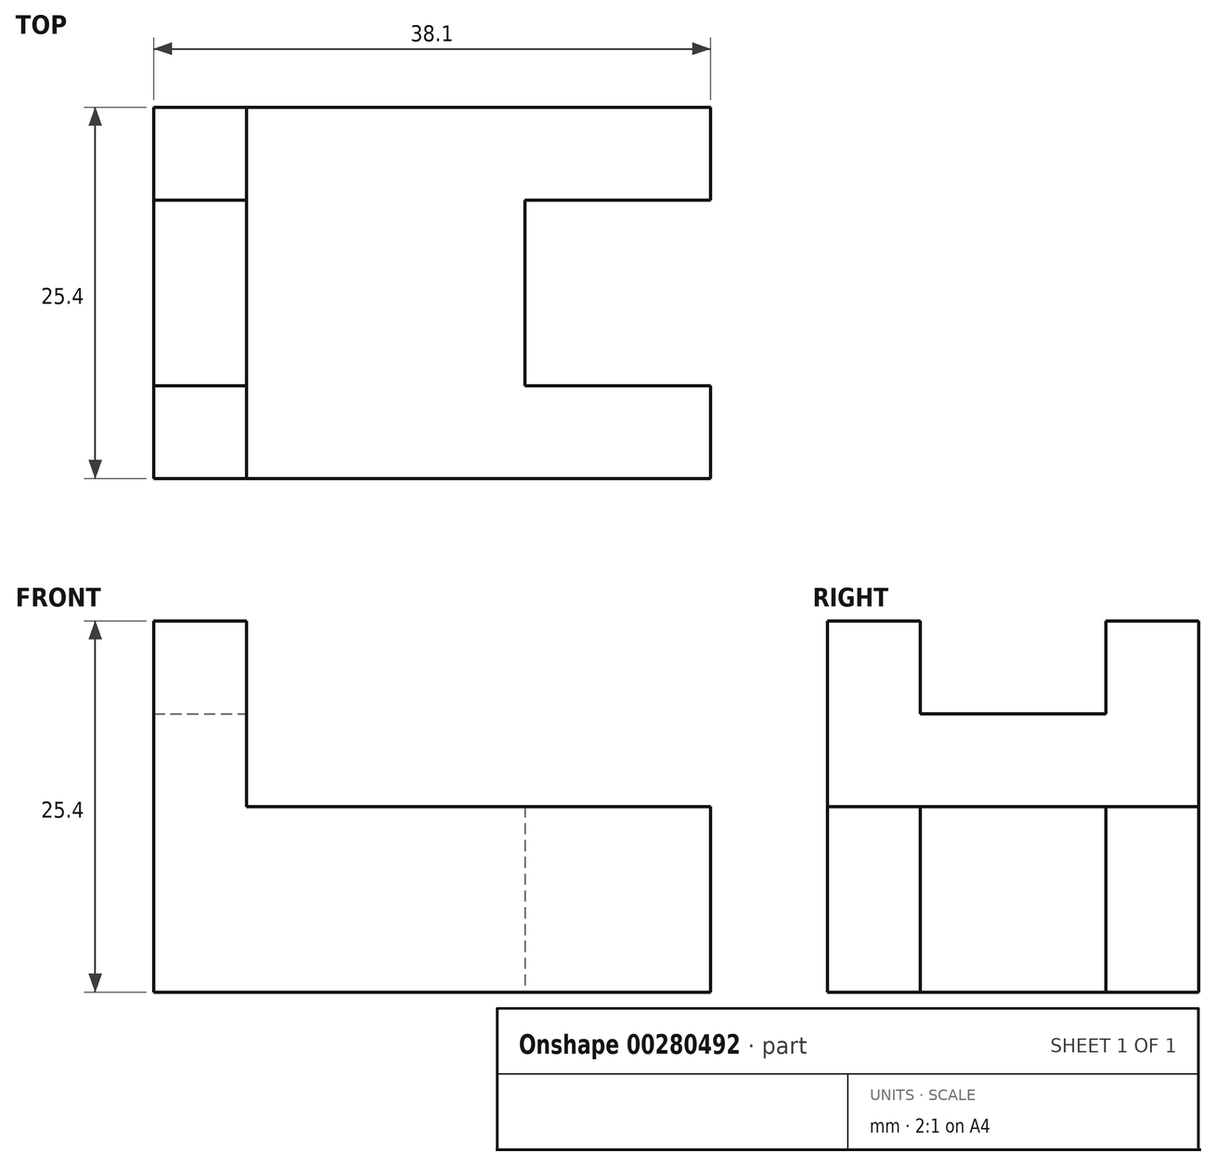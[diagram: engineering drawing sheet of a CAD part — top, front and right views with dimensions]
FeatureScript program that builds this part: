
annotation { "Feature Type Name" : "Feature", "Feature Type Description" : "" }
export const myFeature = defineFeature(function(context is Context, id is Id, definition is map)
    precondition{}
    {
        {
            var Q0;
            Q0=qCreatedBy(makeId("Front.planeOp"),FACE);
            var sketch = newSketch(context, id + "F0", { "sketchPlane" : qUnion([Q0])});
            skLineSegment(sketch, "E0", {"start": v(-19.05, 0) * mm, "end": v(19.05, 0) * mm});
            skLineSegment(sketch, "E1", {"start": v(19.05, 0) * mm, "end": v(19.05, 12.7) * mm});
            skLineSegment(sketch, "E2", {"start": v(19.05, 12.7) * mm, "end": v(-12.7, 12.7) * mm});
            skLineSegment(sketch, "E3", {"start": v(-12.7, 12.7) * mm, "end": v(-12.7, 25.4) * mm});
            skLineSegment(sketch, "E4", {"start": v(-12.7, 25.4) * mm, "end": v(-19.05, 25.4) * mm});
            skLineSegment(sketch, "E5", {"start": v(-19.05, 25.4) * mm, "end": v(-19.05, 0) * mm});
            skLineSegment(sketch, "E6", {"start": v(-19.05, 19.05) * mm, "end": v(-12.7, 19.05) * mm});
            skLineSegment(sketch, "E7", {"start": v(6.35, 12.7) * mm, "end": v(6.35, 0) * mm});
            skSolve(sketch);
        }
        {
            var Q0;
            {var subQ3=sQuery(id+"F0.wireOp",EDGE,"E6");Q0=makeQuery(id+"F0.imprint","IMPRINT",FACE,{"disambiguationData":[TD([[makeQuery(id+"F0.imprint","IMPRINT",EDGE,{"derivedFrom":subQ3}),-1.0]])]});}
            var Q1;
            {var subQ0=sQuery(id+"F0.wireOp",EDGE,"E4");Q1=makeQuery(id+"F0.imprint","IMPRINT",FACE,{"disambiguationData":[TD([[makeQuery(id+"F0.imprint","IMPRINT",EDGE,{"derivedFrom":subQ0}),1.0]])]});}
            var Q2;
            {var subQ0=sQuery(id+"F0.wireOp",EDGE,"E1");Q2=makeQuery(id+"F0.imprint","IMPRINT",FACE,{"disambiguationData":[TD([[makeQuery(id+"F0.imprint","IMPRINT",EDGE,{"derivedFrom":subQ0}),1.0]])]});}
            extrude(context, id + "F1", {"entities" : qUnion([Q0, Q1, Q2]), "endBound" : BoundingType.SYMMETRIC, "depth" : 25.4 * mm});
        }
        {
            var Q0;
            Q0=makeQuery(id+"F0.imprint","IMPRINT",FACE,{"disambiguationData":[TD([[makeQuery(id+"F0.imprint","IMPRINT",EDGE,{"derivedFrom":sQuery(id+"F0.wireOp",EDGE,"E0")}),1.0]])]});
            var Q1;
            {var subQ0=sQuery(id+"F0.wireOp",EDGE,"E4");Q1=makeQuery(id+"F0.imprint","IMPRINT",FACE,{"disambiguationData":[TD([[makeQuery(id+"F0.imprint","IMPRINT",EDGE,{"derivedFrom":subQ0}),1.0]])]});}
            extrude(context, id + "F2", {"entities" : qUnion([Q0, Q1]), "operationType" : NewBodyOperationType.REMOVE, "endBound" : BoundingType.SYMMETRIC, "depth" : 12.7 * mm});
        }
    });
